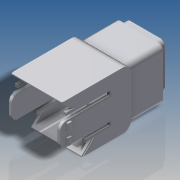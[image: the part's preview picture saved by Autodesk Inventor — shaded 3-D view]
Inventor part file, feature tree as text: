
AUTODESK INVENTOR PART (.ipt)
format: ipt  version: 2016 SP2 (Build 200236200, 236)  size: 589,312 bytes
history: native  units: in
note: dims shown in document units (in); Inventor stores cm internally (conversion verified against a paired STEP export)
features: extrude x8, sketch x4, mirror x1, plane x1, fillet x1
ambient origin geometry x8: Origin, YZ Plane, XZ Plane, XY Plane, X Axis, Y Axis, Z Axis, Center Point
bodies: Solid1 (feature_tree)
feature tree (15):
  sketch  "Sketch2"  dims[d0=0.2205in d1=0.2205in]
  extrude  "Extrusion1"  Depth=0.2205in
  extrude  "Extrusion2"  Depth=0.0157in
  sketch  "Sketch3"  dims[d2=0.0472in d3=0.0157in]
  extrude  "Extrusion3"  Depth=1.1024in
  extrude  "Extrusion4"  Depth=0.0039in
  mirror  "Mirror1"
  plane  "Work Plane1"
  sketch  "Sketch4"  dims[d4=45.0deg d5=1.1024in]
  extrude  "Extrusion5"  Depth=0.0039in
  extrude  "Extrusion6"  Depth=0.0039in
  sketch  "Sketch5"  dims[d6=0.7874in d7=0.3465in d8=0.9134in d9=0.0472in d10=0.063in d11=0.1417in d12=0.6929in d13=0.3937in d14=1.1339in d15=0.0945in d16=0.0472in d17=0.0472in d18=0.0787in d19=0.8189in d20=0.0in d21=0.7244in d22=0.0in d23=0.0315in d24=0.1102in d25=0.063in d26=0.0945in d27=0.0945in d28=0.0079in d29=0.0in d30=0.0315in d31=0.0in d32=0.5354in d33=0.0787in d34=0.0787in d35=0.0378in d36=0.0945in d37=0.0787in d38=0.8189in d39=0.7087in d40=0.5732in d41=0.5732in d42=0.4094in d43=0.4724in d44=0.0787in d45=0.6299in d46=0.7559in d47=0.0945in d48=0.0315in d49=0.0in d50=0.0945in d51=0.0in d52=0.7244in d53=0.6299in d54=0.5669in d55=0.6299in d56=0.5512in d57=0.0in d58=0.6142in d59=0.0in d60=0.0039in]
  extrude  "Extrusion7"  Depth=0.063in
  extrude  "Extrusion8"  Depth=0.0039in
  fillet  "Fillet1"  Radius=0.6929in
